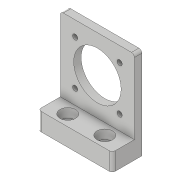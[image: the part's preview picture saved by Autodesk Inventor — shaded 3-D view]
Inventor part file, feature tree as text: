
AUTODESK INVENTOR PART (.ipt)
format: ipt  version: 2021 (Build 250183000, 183)  size: 152,064 bytes
history: native  units: mm
features: sketch x3, hole x3, extrude x2, plane x1, fillet x1
ambient origin geometry x8: Origin, YZ Plane, XZ Plane, XY Plane, X Axis, Y Axis, Z Axis, Center Point
bodies: Solid1 (feature_tree)
feature tree (10):
  sketch  "Sketch1"  dims[d0=32.0mm d1=50.0mm]
  extrude  "Extrusion1"  Depth=50.0mm
  hole  "Hole1"  [1 undecoded]
  plane  "Work Plane1"
  sketch  "Sketch2"  dims[d2=50.0mm d3=20.0mm d5=30.0mm d6=20.0mm d8=30.0mm]
  extrude  "Extrusion2"  [1 undecoded]
  hole  "Hole2"  [1 undecoded]
  fillet  "Fillet1"  Radius=20.0mm
  hole  "Hole4"  [1 undecoded]
  sketch  "Sketch5"  dims[d11=5.0mm d12=0.0mm d13=3.5mm d14=6.0mm d15=4.0mm d16=2.0mm d17=90.0deg d18=8.0mm d19=20.594885mm d20=-37.0mm d21=20.0mm d22=20.0mm d24=25.0mm d25=10.0mm d27=10.0mm d29=5.0mm d30=0.0mm d31=6.5mm d32=6.0mm d33=4.0mm d34=2.0mm d35=90.0deg d36=8.0mm d37=20.594885mm d38=2.0mm d46=12.5mm d47=10.5mm d48=6.0mm d49=4.0mm d50=2.0mm d51=90.0deg d52=6.2mm d53=0.0mm]
note: 4 required parameter values undecoded (feature->parameter linkage not recoverable at this tier; creation-order binding heuristic only, values carry confidence <= 0.55)
